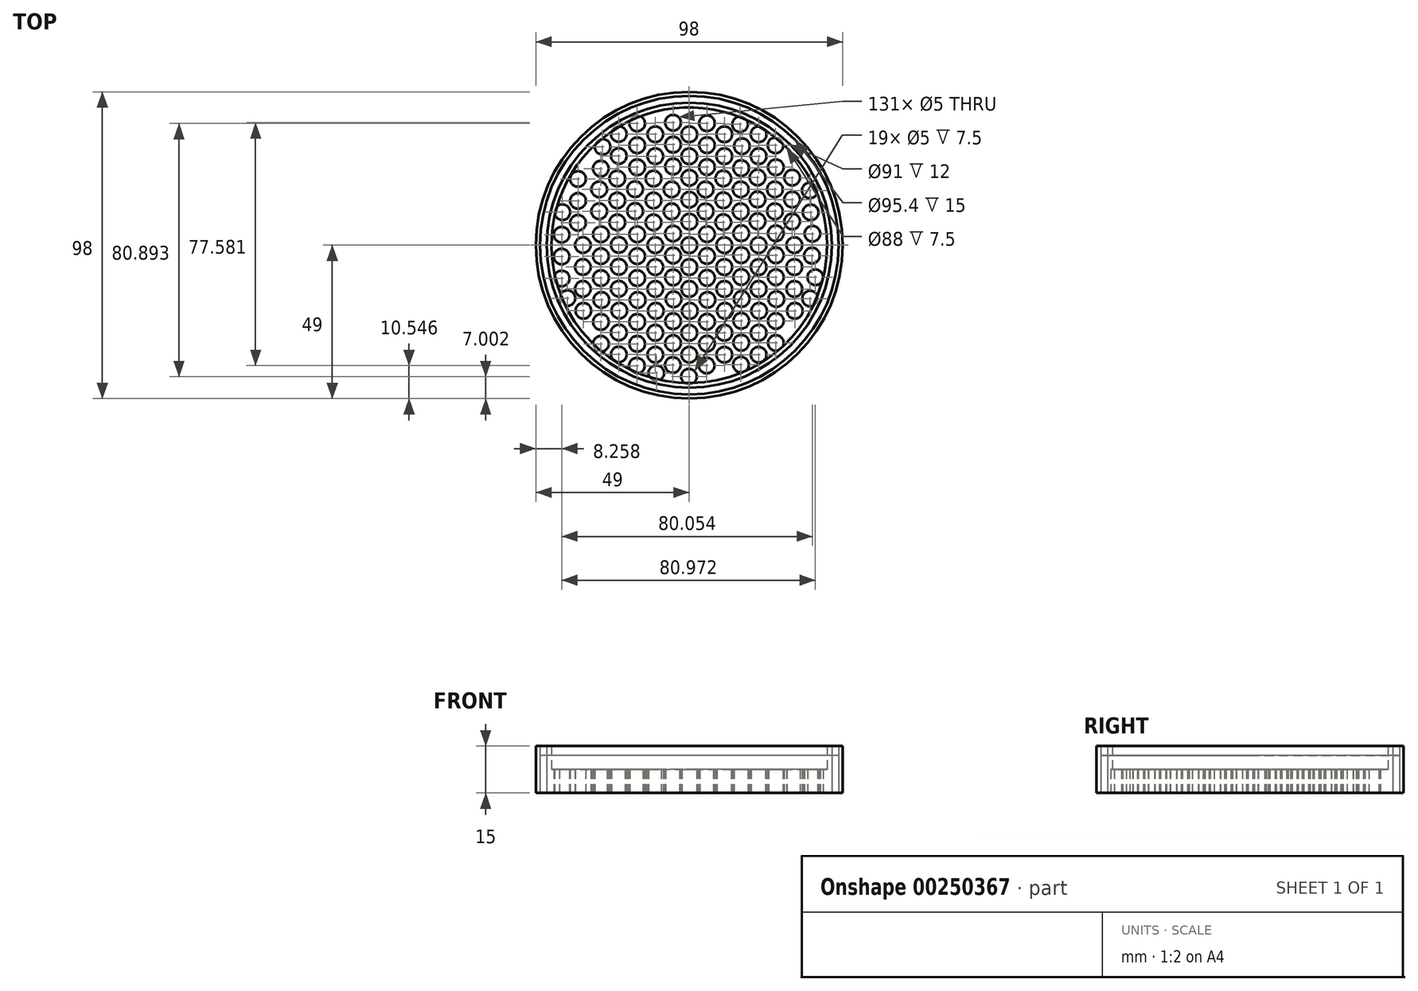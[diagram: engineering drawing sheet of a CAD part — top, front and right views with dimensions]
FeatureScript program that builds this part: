
annotation { "Feature Type Name" : "Feature", "Feature Type Description" : "" }
export const myFeature = defineFeature(function(context is Context, id is Id, definition is map)
    precondition{}
    {
        {
            var Q0;
            Q0=qCreatedBy(makeId("Top.planeOp"),FACE);
            var sketch = newSketch(context, id + "F0", { "sketchPlane" : qUnion([Q0])});
            skCircle(sketch, "E0", {"center": v(0, 0) * mm, "radius": 49 * mm});
            skCircle(sketch, "E1", {"center": v(0, 0) * mm, "radius": 45.5 * mm});
            skCircle(sketch, "E2", {"center": v(0, 0) * mm, "radius": 47.7 * mm});
            skCircle(sketch, "E3", {"center": v(0, 0) * mm, "radius": 44 * mm});
            skSolve(sketch);
        }
        {
            var Q0;
            Q0 = qSketchRegion(id + "F0", true);
            var Q1;
            Q1=makeQuery(id+"F0.imprint","IMPRINT",FACE,{"disambiguationData":[TD([[makeQuery(id+"F0.imprint","IMPRINT",EDGE,{"derivedFrom":sQuery(id+"F0.wireOp",EDGE,"E1")}),1.0]])]});
            extrude(context, id + "F1", {"entities" : qUnion([Q0, Q1]), "depth" : 15 * mm});
        }
        {
            var Q0;
            Q0=makeQuery(id+"F0.imprint","IMPRINT",FACE,{"disambiguationData":[TD([[makeQuery(id+"F0.imprint","IMPRINT",EDGE,{"derivedFrom":sQuery(id+"F0.wireOp",EDGE,"E1")}),-1.0]])]});
            extrude(context, id + "F2", {"entities" : qUnion([Q0]), "depth" : 12 * mm});
        }
        {
            var Q0;
            Q0=makeQuery(id+"F0.imprint","IMPRINT",FACE,{"disambiguationData":[TD([[makeQuery(id+"F0.imprint","IMPRINT",EDGE,{"derivedFrom":sQuery(id+"F0.wireOp",EDGE,"E3")}),1.0]])]});
            extrude(context, id + "F3", {"entities" : qUnion([Q0]), "operationType" : NewBodyOperationType.ADD, "depth" : 7.5 * mm});
        }
        {
            var Q0;
            Q0=qCreatedBy(makeId("Top.planeOp"),FACE);
            var sketch = newSketch(context, id + "F4", { "sketchPlane" : qUnion([Q0])});
            skCircle(sketch, "E4", {"center": v(0, 0) * mm, "radius": 2.5 * mm});
            skCircle(sketch, "E5", {"center": v(0, -7) * mm, "radius": 2.5 * mm});
            skCircle(sketch, "E6", {"center": v(0, -14) * mm, "radius": 2.5 * mm});
            skCircle(sketch, "E7", {"center": v(0.16, -21) * mm, "radius": 2.5 * mm});
            skCircle(sketch, "E8", {"center": v(0, -28) * mm, "radius": 2.5 * mm});
            skCircle(sketch, "E9", {"center": v(0, -35) * mm, "radius": 2.5 * mm});
            skCircle(sketch, "E10", {"center": v(-0.1, -42) * mm, "radius": 2.5 * mm});
            skCircle(sketch, "E11", {"center": v(5.64, 3.54) * mm, "radius": 2.5 * mm});
            skCircle(sketch, "E12", {"center": v(5.64, -3.46) * mm, "radius": 2.5 * mm});
            skCircle(sketch, "E13", {"center": v(5.64, -10.46) * mm, "radius": 2.5 * mm});
            skCircle(sketch, "E14", {"center": v(5.8, -17.45) * mm, "radius": 2.5 * mm});
            skCircle(sketch, "E15", {"center": v(5.64, -24.45) * mm, "radius": 2.5 * mm});
            skCircle(sketch, "E16", {"center": v(5.64, -31.45) * mm, "radius": 2.5 * mm});
            skCircle(sketch, "E17", {"center": v(5.55, -38.45) * mm, "radius": 2.5 * mm});
            skCircle(sketch, "E18", {"center": v(-5.18, 3.72) * mm, "radius": 2.5 * mm});
            skCircle(sketch, "E19", {"center": v(-5.18, -3.28) * mm, "radius": 2.5 * mm});
            skCircle(sketch, "E20", {"center": v(-5.18, -10.28) * mm, "radius": 2.5 * mm});
            skCircle(sketch, "E21", {"center": v(-5.02, -17.28) * mm, "radius": 2.5 * mm});
            skCircle(sketch, "E22", {"center": v(-5.18, -24.28) * mm, "radius": 2.5 * mm});
            skCircle(sketch, "E23", {"center": v(-5.18, -31.28) * mm, "radius": 2.5 * mm});
            skCircle(sketch, "E24", {"center": v(-5.28, -38.28) * mm, "radius": 2.5 * mm});
            skCircle(sketch, "E25", {"center": v(11.2, 0.01) * mm, "radius": 2.5 * mm});
            skCircle(sketch, "E26", {"center": v(11.2, -6.99) * mm, "radius": 2.5 * mm});
            skCircle(sketch, "E27", {"center": v(11.2, -13.99) * mm, "radius": 2.5 * mm});
            skCircle(sketch, "E28", {"center": v(11.36, -20.98) * mm, "radius": 2.5 * mm});
            skCircle(sketch, "E29", {"center": v(11.2, -27.98) * mm, "radius": 2.5 * mm});
            skCircle(sketch, "E30", {"center": v(11.2, -34.98) * mm, "radius": 2.5 * mm});
            skCircle(sketch, "E31", {"center": v(16.58, 3.83) * mm, "radius": 2.5 * mm});
            skCircle(sketch, "E32", {"center": v(16.58, -3.17) * mm, "radius": 2.5 * mm});
            skCircle(sketch, "E33", {"center": v(16.58, -10.17) * mm, "radius": 2.5 * mm});
            skCircle(sketch, "E34", {"center": v(16.74, -17.17) * mm, "radius": 2.5 * mm});
            skCircle(sketch, "E35", {"center": v(16.58, -24.17) * mm, "radius": 2.5 * mm});
            skCircle(sketch, "E36", {"center": v(16.58, -31.17) * mm, "radius": 2.5 * mm});
            skCircle(sketch, "E37", {"center": v(16.48, -38.16) * mm, "radius": 2.5 * mm});
            skCircle(sketch, "E38", {"center": v(22.14, 0.01) * mm, "radius": 2.5 * mm});
            skCircle(sketch, "E39", {"center": v(22.14, -6.99) * mm, "radius": 2.5 * mm});
            skCircle(sketch, "E40", {"center": v(22.14, -13.99) * mm, "radius": 2.5 * mm});
            skCircle(sketch, "E41", {"center": v(22.3, -20.98) * mm, "radius": 2.5 * mm});
            skCircle(sketch, "E42", {"center": v(22.14, -27.98) * mm, "radius": 2.5 * mm});
            skCircle(sketch, "E43", {"center": v(22.14, -34.98) * mm, "radius": 2.5 * mm});
            skCircle(sketch, "E44", {"center": v(27.64, 3.78) * mm, "radius": 2.5 * mm});
            skCircle(sketch, "E45", {"center": v(27.64, -3.22) * mm, "radius": 2.5 * mm});
            skCircle(sketch, "E46", {"center": v(27.64, -10.22) * mm, "radius": 2.5 * mm});
            skCircle(sketch, "E47", {"center": v(27.8, -17.22) * mm, "radius": 2.5 * mm});
            skCircle(sketch, "E48", {"center": v(27.64, -24.22) * mm, "radius": 2.5 * mm});
            skCircle(sketch, "E49", {"center": v(27.64, -31.22) * mm, "radius": 2.5 * mm});
            skCircle(sketch, "E50", {"center": v(33.54, 0.01) * mm, "radius": 2.5 * mm});
            skCircle(sketch, "E51", {"center": v(33.54, -6.99) * mm, "radius": 2.5 * mm});
            skCircle(sketch, "E52", {"center": v(33.54, -13.99) * mm, "radius": 2.5 * mm});
            skCircle(sketch, "E53", {"center": v(33.7, -20.98) * mm, "radius": 2.5 * mm});
            skCircle(sketch, "E54", {"center": v(39.31, 3.67) * mm, "radius": 2.5 * mm});
            skCircle(sketch, "E55", {"center": v(39.15, -3.33) * mm, "radius": 2.5 * mm});
            skCircle(sketch, "E56", {"center": v(40.23, -10.25) * mm, "radius": 2.5 * mm});
            skCircle(sketch, "E57", {"center": v(38.57, -17.05) * mm, "radius": 2.5 * mm});
            skCircle(sketch, "E58", {"center": v(-10.85, 0.01) * mm, "radius": 2.5 * mm});
            skCircle(sketch, "E59", {"center": v(-10.85, -6.99) * mm, "radius": 2.5 * mm});
            skCircle(sketch, "E60", {"center": v(-10.85, -13.99) * mm, "radius": 2.5 * mm});
            skCircle(sketch, "E61", {"center": v(-10.69, -20.98) * mm, "radius": 2.5 * mm});
            skCircle(sketch, "E62", {"center": v(-10.85, -27.98) * mm, "radius": 2.5 * mm});
            skCircle(sketch, "E63", {"center": v(-10.85, -34.98) * mm, "radius": 2.5 * mm});
            skCircle(sketch, "E64", {"center": v(-16.63, 3.49) * mm, "radius": 2.5 * mm});
            skCircle(sketch, "E65", {"center": v(-16.63, -3.51) * mm, "radius": 2.5 * mm});
            skCircle(sketch, "E66", {"center": v(-16.63, -10.51) * mm, "radius": 2.5 * mm});
            skCircle(sketch, "E67", {"center": v(-16.47, -17.51) * mm, "radius": 2.5 * mm});
            skCircle(sketch, "E68", {"center": v(-16.63, -24.51) * mm, "radius": 2.5 * mm});
            skCircle(sketch, "E69", {"center": v(-16.63, -31.51) * mm, "radius": 2.5 * mm});
            skCircle(sketch, "E70", {"center": v(-16.73, -38.51) * mm, "radius": 2.5 * mm});
            skCircle(sketch, "E71", {"center": v(-22.5, 0.1) * mm, "radius": 2.5 * mm});
            skCircle(sketch, "E72", {"center": v(-22.5, -6.9) * mm, "radius": 2.5 * mm});
            skCircle(sketch, "E73", {"center": v(-22.5, -13.9) * mm, "radius": 2.5 * mm});
            skCircle(sketch, "E74", {"center": v(-22.34, -20.9) * mm, "radius": 2.5 * mm});
            skCircle(sketch, "E75", {"center": v(-22.5, -27.9) * mm, "radius": 2.5 * mm});
            skCircle(sketch, "E76", {"center": v(-22.5, -34.9) * mm, "radius": 2.5 * mm});
            skCircle(sketch, "E77", {"center": v(-28.21, 3.49) * mm, "radius": 2.5 * mm});
            skCircle(sketch, "E78", {"center": v(-28.21, -3.51) * mm, "radius": 2.5 * mm});
            skCircle(sketch, "E79", {"center": v(-28.21, -10.51) * mm, "radius": 2.5 * mm});
            skCircle(sketch, "E80", {"center": v(-28.05, -17.51) * mm, "radius": 2.5 * mm});
            skCircle(sketch, "E81", {"center": v(-28.21, -24.51) * mm, "radius": 2.5 * mm});
            skCircle(sketch, "E82", {"center": v(-28.21, -31.51) * mm, "radius": 2.5 * mm});
            skCircle(sketch, "E83", {"center": v(-33.98, 0.04) * mm, "radius": 2.5 * mm});
            skCircle(sketch, "E84", {"center": v(-33.98, -6.96) * mm, "radius": 2.5 * mm});
            skCircle(sketch, "E85", {"center": v(-33.98, -13.96) * mm, "radius": 2.5 * mm});
            skCircle(sketch, "E86", {"center": v(-33.82, -20.96) * mm, "radius": 2.5 * mm});
            skCircle(sketch, "E87", {"center": v(-40.74, 3.36) * mm, "radius": 2.5 * mm});
            skCircle(sketch, "E88", {"center": v(-40.74, -3.64) * mm, "radius": 2.5 * mm});
            skCircle(sketch, "E89", {"center": v(-40.74, -10.64) * mm, "radius": 2.5 * mm});
            skCircle(sketch, "E90", {"center": v(-10.53, -40.88) * mm, "radius": 2.5 * mm});
            skCircle(sketch, "E91", {"center": v(5.21, 17.8) * mm, "radius": 2.5 * mm});
            skCircle(sketch, "E92", {"center": v(5.21, 10.8) * mm, "radius": 2.5 * mm});
            skCircle(sketch, "E93", {"center": v(10.86, 21.34) * mm, "radius": 2.5 * mm});
            skCircle(sketch, "E94", {"center": v(10.86, 14.34) * mm, "radius": 2.5 * mm});
            skCircle(sketch, "E95", {"center": v(10.86, 7.34) * mm, "radius": 2.5 * mm});
            skCircle(sketch, "E96", {"center": v(0.03, 21.51) * mm, "radius": 2.5 * mm});
            skCircle(sketch, "E97", {"center": v(0.03, 14.51) * mm, "radius": 2.5 * mm});
            skCircle(sketch, "E98", {"center": v(0.03, 7.51) * mm, "radius": 2.5 * mm});
            skCircle(sketch, "E99", {"center": v(16.41, 17.8) * mm, "radius": 2.5 * mm});
            skCircle(sketch, "E100", {"center": v(16.41, 10.8) * mm, "radius": 2.5 * mm});
            skCircle(sketch, "E101", {"center": v(21.8, 21.63) * mm, "radius": 2.5 * mm});
            skCircle(sketch, "E102", {"center": v(21.8, 14.63) * mm, "radius": 2.5 * mm});
            skCircle(sketch, "E103", {"center": v(21.8, 7.63) * mm, "radius": 2.5 * mm});
            skCircle(sketch, "E104", {"center": v(27.35, 17.8) * mm, "radius": 2.5 * mm});
            skCircle(sketch, "E105", {"center": v(27.35, 10.8) * mm, "radius": 2.5 * mm});
            skCircle(sketch, "E106", {"center": v(32.85, 21.57) * mm, "radius": 2.5 * mm});
            skCircle(sketch, "E107", {"center": v(32.85, 14.57) * mm, "radius": 2.5 * mm});
            skCircle(sketch, "E108", {"center": v(32.85, 7.57) * mm, "radius": 2.5 * mm});
            skCircle(sketch, "E109", {"center": v(38.49, 17.5) * mm, "radius": 2.5 * mm});
            skCircle(sketch, "E110", {"center": v(38.75, 10.5) * mm, "radius": 2.5 * mm});
            skCircle(sketch, "E111", {"center": v(-5.64, 17.8) * mm, "radius": 2.5 * mm});
            skCircle(sketch, "E112", {"center": v(-5.64, 10.8) * mm, "radius": 2.5 * mm});
            skCircle(sketch, "E113", {"center": v(-11.42, 21.28) * mm, "radius": 2.5 * mm});
            skCircle(sketch, "E114", {"center": v(-11.42, 14.28) * mm, "radius": 2.5 * mm});
            skCircle(sketch, "E115", {"center": v(-11.42, 7.28) * mm, "radius": 2.5 * mm});
            skCircle(sketch, "E116", {"center": v(-17.3, 17.89) * mm, "radius": 2.5 * mm});
            skCircle(sketch, "E117", {"center": v(-17.3, 10.89) * mm, "radius": 2.5 * mm});
            skCircle(sketch, "E118", {"center": v(-23, 21.28) * mm, "radius": 2.5 * mm});
            skCircle(sketch, "E119", {"center": v(-23, 14.28) * mm, "radius": 2.5 * mm});
            skCircle(sketch, "E120", {"center": v(-23, 7.28) * mm, "radius": 2.5 * mm});
            skCircle(sketch, "E121", {"center": v(-28.77, 17.84) * mm, "radius": 2.5 * mm});
            skCircle(sketch, "E122", {"center": v(-28.77, 10.84) * mm, "radius": 2.5 * mm});
            skCircle(sketch, "E123", {"center": v(-35.53, 21.16) * mm, "radius": 2.5 * mm});
            skCircle(sketch, "E124", {"center": v(-35.53, 14.16) * mm, "radius": 2.5 * mm});
            skCircle(sketch, "E125", {"center": v(-35.53, 7.16) * mm, "radius": 2.5 * mm});
            skCircle(sketch, "E126", {"center": v(0, 35.4) * mm, "radius": 2.5 * mm});
            skCircle(sketch, "E127", {"center": v(0, 28.4) * mm, "radius": 2.5 * mm});
            skCircle(sketch, "E128", {"center": v(5.64, 38.95) * mm, "radius": 2.5 * mm});
            skCircle(sketch, "E129", {"center": v(5.64, 31.95) * mm, "radius": 2.5 * mm});
            skCircle(sketch, "E130", {"center": v(5.64, 24.95) * mm, "radius": 2.5 * mm});
            skCircle(sketch, "E131", {"center": v(-5.18, 39.13) * mm, "radius": 2.5 * mm});
            skCircle(sketch, "E132", {"center": v(-5.18, 32.13) * mm, "radius": 2.5 * mm});
            skCircle(sketch, "E133", {"center": v(-5.18, 25.13) * mm, "radius": 2.5 * mm});
            skCircle(sketch, "E134", {"center": v(11.2, 35.42) * mm, "radius": 2.5 * mm});
            skCircle(sketch, "E135", {"center": v(11.2, 28.42) * mm, "radius": 2.5 * mm});
            skCircle(sketch, "E136", {"center": v(16.2, 38.63) * mm, "radius": 2.5 * mm});
            skCircle(sketch, "E137", {"center": v(16.8, 31.63) * mm, "radius": 2.5 * mm});
            skCircle(sketch, "E138", {"center": v(16.56, 24.64) * mm, "radius": 2.5 * mm});
            skCircle(sketch, "E139", {"center": v(22.13, 35.42) * mm, "radius": 2.5 * mm});
            skCircle(sketch, "E140", {"center": v(22.13, 28.42) * mm, "radius": 2.5 * mm});
            skCircle(sketch, "E141", {"center": v(27.52, 31.9) * mm, "radius": 2.5 * mm});
            skCircle(sketch, "E142", {"center": v(27.64, 24.9) * mm, "radius": 2.5 * mm});
            skCircle(sketch, "E143", {"center": v(-10.85, 35.42) * mm, "radius": 2.5 * mm});
            skCircle(sketch, "E144", {"center": v(-10.85, 28.42) * mm, "radius": 2.5 * mm});
            skCircle(sketch, "E145", {"center": v(-16.64, 38.9) * mm, "radius": 2.5 * mm});
            skCircle(sketch, "E146", {"center": v(-16.64, 31.9) * mm, "radius": 2.5 * mm});
            skCircle(sketch, "E147", {"center": v(-16.64, 24.9) * mm, "radius": 2.5 * mm});
            skCircle(sketch, "E148", {"center": v(-22.5, 35.5) * mm, "radius": 2.5 * mm});
            skCircle(sketch, "E149", {"center": v(-22.5, 28.5) * mm, "radius": 2.5 * mm});
            skCircle(sketch, "E150", {"center": v(-27.7, 31.44) * mm, "radius": 2.5 * mm});
            skCircle(sketch, "E151", {"center": v(-28.25, 24.46) * mm, "radius": 2.5 * mm});
            skCircle(sketch, "E152", {"center": v(-38.9, -16.92) * mm, "radius": 2.5 * mm});
            skCircle(sketch, "E153", {"center": v(-40.55, 10.56) * mm, "radius": 2.5 * mm});
            skSolve(sketch);
        }
        {
            var Q0;
            Q0=makeQuery(id+"F4.imprint","IMPRINT",FACE,{"disambiguationData":[TD([[makeQuery(id+"F4.imprint","IMPRINT",EDGE,{"derivedFrom":sQuery(id+"F4.wireOp",EDGE,"E39")}),1.0]])]});
            var Q1;
            Q1=makeQuery(id+"F4.imprint","IMPRINT",FACE,{"disambiguationData":[TD([[makeQuery(id+"F4.imprint","IMPRINT",EDGE,{"derivedFrom":sQuery(id+"F4.wireOp",EDGE,"E145")}),1.0]])]});
            var Q2;
            Q2=makeQuery(id+"F4.imprint","IMPRINT",FACE,{"disambiguationData":[TD([[makeQuery(id+"F4.imprint","IMPRINT",EDGE,{"derivedFrom":sQuery(id+"F4.wireOp",EDGE,"E23")}),1.0]])]});
            var Q3;
            Q3=makeQuery(id+"F4.imprint","IMPRINT",FACE,{"disambiguationData":[TD([[makeQuery(id+"F4.imprint","IMPRINT",EDGE,{"derivedFrom":sQuery(id+"F4.wireOp",EDGE,"E41")}),1.0]])]});
            var Q4;
            Q4=makeQuery(id+"F4.imprint","IMPRINT",FACE,{"disambiguationData":[TD([[makeQuery(id+"F4.imprint","IMPRINT",EDGE,{"derivedFrom":sQuery(id+"F4.wireOp",EDGE,"E119")}),1.0]])]});
            var Q5;
            Q5=makeQuery(id+"F4.imprint","IMPRINT",FACE,{"disambiguationData":[TD([[makeQuery(id+"F4.imprint","IMPRINT",EDGE,{"derivedFrom":sQuery(id+"F4.wireOp",EDGE,"E87")}),1.0]])]});
            var Q6;
            Q6=makeQuery(id+"F4.imprint","IMPRINT",FACE,{"disambiguationData":[TD([[makeQuery(id+"F4.imprint","IMPRINT",EDGE,{"derivedFrom":sQuery(id+"F4.wireOp",EDGE,"E71")}),1.0]])]});
            var Q7;
            Q7=makeQuery(id+"F4.imprint","IMPRINT",FACE,{"disambiguationData":[TD([[makeQuery(id+"F4.imprint","IMPRINT",EDGE,{"derivedFrom":sQuery(id+"F4.wireOp",EDGE,"E21")}),1.0]])]});
            var Q8;
            Q8=makeQuery(id+"F4.imprint","IMPRINT",FACE,{"disambiguationData":[TD([[makeQuery(id+"F4.imprint","IMPRINT",EDGE,{"derivedFrom":sQuery(id+"F4.wireOp",EDGE,"E135")}),1.0]])]});
            var Q9;
            Q9=makeQuery(id+"F4.imprint","IMPRINT",FACE,{"disambiguationData":[TD([[makeQuery(id+"F4.imprint","IMPRINT",EDGE,{"derivedFrom":sQuery(id+"F4.wireOp",EDGE,"E151")}),1.0]])]});
            var Q10;
            Q10=makeQuery(id+"F4.imprint","IMPRINT",FACE,{"disambiguationData":[TD([[makeQuery(id+"F4.imprint","IMPRINT",EDGE,{"derivedFrom":sQuery(id+"F4.wireOp",EDGE,"E36")}),1.0]])]});
            var Q11;
            Q11=makeQuery(id+"F4.imprint","IMPRINT",FACE,{"disambiguationData":[TD([[makeQuery(id+"F4.imprint","IMPRINT",EDGE,{"derivedFrom":sQuery(id+"F4.wireOp",EDGE,"E132")}),1.0]])]});
            var Q12;
            Q12=makeQuery(id+"F4.imprint","IMPRINT",FACE,{"disambiguationData":[TD([[makeQuery(id+"F4.imprint","IMPRINT",EDGE,{"derivedFrom":sQuery(id+"F4.wireOp",EDGE,"E37")}),1.0]])]});
            var Q13;
            Q13=makeQuery(id+"F4.imprint","IMPRINT",FACE,{"disambiguationData":[TD([[makeQuery(id+"F4.imprint","IMPRINT",EDGE,{"derivedFrom":sQuery(id+"F4.wireOp",EDGE,"E148")}),1.0]])]});
            var Q14;
            Q14=makeQuery(id+"F4.imprint","IMPRINT",FACE,{"disambiguationData":[TD([[makeQuery(id+"F4.imprint","IMPRINT",EDGE,{"derivedFrom":sQuery(id+"F4.wireOp",EDGE,"E53")}),1.0]])]});
            var Q15;
            Q15=makeQuery(id+"F4.imprint","IMPRINT",FACE,{"disambiguationData":[TD([[makeQuery(id+"F4.imprint","IMPRINT",EDGE,{"derivedFrom":sQuery(id+"F4.wireOp",EDGE,"E73")}),1.0]])]});
            var Q16;
            Q16=makeQuery(id+"F4.imprint","IMPRINT",FACE,{"disambiguationData":[TD([[makeQuery(id+"F4.imprint","IMPRINT",EDGE,{"derivedFrom":sQuery(id+"F4.wireOp",EDGE,"E105")}),1.0]])]});
            var Q17;
            Q17=makeQuery(id+"F4.imprint","IMPRINT",FACE,{"disambiguationData":[TD([[makeQuery(id+"F4.imprint","IMPRINT",EDGE,{"derivedFrom":sQuery(id+"F4.wireOp",EDGE,"E68")}),1.0]])]});
            var Q18;
            Q18=makeQuery(id+"F4.imprint","IMPRINT",FACE,{"disambiguationData":[TD([[makeQuery(id+"F4.imprint","IMPRINT",EDGE,{"derivedFrom":sQuery(id+"F4.wireOp",EDGE,"E84")}),1.0]])]});
            var Q19;
            Q19=makeQuery(id+"F4.imprint","IMPRINT",FACE,{"disambiguationData":[TD([[makeQuery(id+"F4.imprint","IMPRINT",EDGE,{"derivedFrom":sQuery(id+"F4.wireOp",EDGE,"E103")}),1.0]])]});
            var Q20;
            Q20=makeQuery(id+"F4.imprint","IMPRINT",FACE,{"disambiguationData":[TD([[makeQuery(id+"F4.imprint","IMPRINT",EDGE,{"derivedFrom":sQuery(id+"F4.wireOp",EDGE,"E20")}),1.0]])]});
            var Q21;
            Q21=makeQuery(id+"F4.imprint","IMPRINT",FACE,{"disambiguationData":[TD([[makeQuery(id+"F4.imprint","IMPRINT",EDGE,{"derivedFrom":sQuery(id+"F4.wireOp",EDGE,"E116")}),1.0]])]});
            var Q22;
            Q22=makeQuery(id+"F4.imprint","IMPRINT",FACE,{"disambiguationData":[TD([[makeQuery(id+"F4.imprint","IMPRINT",EDGE,{"derivedFrom":sQuery(id+"F4.wireOp",EDGE,"E100")}),1.0]])]});
            var Q23;
            Q23=makeQuery(id+"F4.imprint","IMPRINT",FACE,{"disambiguationData":[TD([[makeQuery(id+"F4.imprint","IMPRINT",EDGE,{"derivedFrom":sQuery(id+"F4.wireOp",EDGE,"E101")}),1.0]])]});
            var Q24;
            Q24=makeQuery(id+"F4.imprint","IMPRINT",FACE,{"disambiguationData":[TD([[makeQuery(id+"F4.imprint","IMPRINT",EDGE,{"derivedFrom":sQuery(id+"F4.wireOp",EDGE,"E89")}),1.0]])]});
            var Q25;
            Q25=makeQuery(id+"F4.imprint","IMPRINT",FACE,{"disambiguationData":[TD([[makeQuery(id+"F4.imprint","IMPRINT",EDGE,{"derivedFrom":sQuery(id+"F4.wireOp",EDGE,"E81")}),1.0]])]});
            var Q26;
            Q26=makeQuery(id+"F4.imprint","IMPRINT",FACE,{"disambiguationData":[TD([[makeQuery(id+"F4.imprint","IMPRINT",EDGE,{"derivedFrom":sQuery(id+"F4.wireOp",EDGE,"E85")}),1.0]])]});
            var Q27;
            Q27=makeQuery(id+"F4.imprint","IMPRINT",FACE,{"disambiguationData":[TD([[makeQuery(id+"F4.imprint","IMPRINT",EDGE,{"derivedFrom":sQuery(id+"F4.wireOp",EDGE,"E153")}),1.0]])]});
            var Q28;
            Q28=makeQuery(id+"F4.imprint","IMPRINT",FACE,{"disambiguationData":[TD([[makeQuery(id+"F4.imprint","IMPRINT",EDGE,{"derivedFrom":sQuery(id+"F4.wireOp",EDGE,"E117")}),1.0]])]});
            var Q29;
            Q29=makeQuery(id+"F4.imprint","IMPRINT",FACE,{"disambiguationData":[TD([[makeQuery(id+"F4.imprint","IMPRINT",EDGE,{"derivedFrom":sQuery(id+"F4.wireOp",EDGE,"E69")}),1.0]])]});
            var Q30;
            Q30=makeQuery(id+"F4.imprint","IMPRINT",FACE,{"disambiguationData":[TD([[makeQuery(id+"F4.imprint","IMPRINT",EDGE,{"derivedFrom":sQuery(id+"F4.wireOp",EDGE,"E149")}),1.0]])]});
            var Q31;
            Q31=makeQuery(id+"F4.imprint","IMPRINT",FACE,{"disambiguationData":[TD([[makeQuery(id+"F4.imprint","IMPRINT",EDGE,{"derivedFrom":sQuery(id+"F4.wireOp",EDGE,"E133")}),1.0]])]});
            var Q32;
            Q32=makeQuery(id+"F4.imprint","IMPRINT",FACE,{"disambiguationData":[TD([[makeQuery(id+"F4.imprint","IMPRINT",EDGE,{"derivedFrom":sQuery(id+"F4.wireOp",EDGE,"E54")}),1.0]])]});
            var Q33;
            Q33=makeQuery(id+"F4.imprint","IMPRINT",FACE,{"disambiguationData":[TD([[makeQuery(id+"F4.imprint","IMPRINT",EDGE,{"derivedFrom":sQuery(id+"F4.wireOp",EDGE,"E38")}),1.0]])]});
            var Q34;
            Q34=makeQuery(id+"F4.imprint","IMPRINT",FACE,{"disambiguationData":[TD([[makeQuery(id+"F4.imprint","IMPRINT",EDGE,{"derivedFrom":sQuery(id+"F4.wireOp",EDGE,"E22")}),1.0]])]});
            var Q35;
            Q35=makeQuery(id+"F4.imprint","IMPRINT",FACE,{"disambiguationData":[TD([[makeQuery(id+"F4.imprint","IMPRINT",EDGE,{"derivedFrom":sQuery(id+"F4.wireOp",EDGE,"E118")}),1.0]])]});
            var Q36;
            Q36=makeQuery(id+"F4.imprint","IMPRINT",FACE,{"disambiguationData":[TD([[makeQuery(id+"F4.imprint","IMPRINT",EDGE,{"derivedFrom":sQuery(id+"F4.wireOp",EDGE,"E86")}),1.0]])]});
            var Q37;
            Q37=makeQuery(id+"F4.imprint","IMPRINT",FACE,{"disambiguationData":[TD([[makeQuery(id+"F4.imprint","IMPRINT",EDGE,{"derivedFrom":sQuery(id+"F4.wireOp",EDGE,"E102")}),1.0]])]});
            var Q38;
            Q38=makeQuery(id+"F4.imprint","IMPRINT",FACE,{"disambiguationData":[TD([[makeQuery(id+"F4.imprint","IMPRINT",EDGE,{"derivedFrom":sQuery(id+"F4.wireOp",EDGE,"E137")}),1.0]])]});
            var Q39;
            Q39=makeQuery(id+"F4.imprint","IMPRINT",FACE,{"disambiguationData":[TD([[makeQuery(id+"F4.imprint","IMPRINT",EDGE,{"derivedFrom":sQuery(id+"F4.wireOp",EDGE,"E65")}),1.0]])]});
            var Q40;
            Q40=makeQuery(id+"F4.imprint","IMPRINT",FACE,{"disambiguationData":[TD([[makeQuery(id+"F4.imprint","IMPRINT",EDGE,{"derivedFrom":sQuery(id+"F4.wireOp",EDGE,"E70")}),1.0]])]});
            var Q41;
            Q41=makeQuery(id+"F4.imprint","IMPRINT",FACE,{"disambiguationData":[TD([[makeQuery(id+"F4.imprint","IMPRINT",EDGE,{"derivedFrom":sQuery(id+"F4.wireOp",EDGE,"E134")}),1.0]])]});
            var Q42;
            Q42=makeQuery(id+"F4.imprint","IMPRINT",FACE,{"disambiguationData":[TD([[makeQuery(id+"F4.imprint","IMPRINT",EDGE,{"derivedFrom":sQuery(id+"F4.wireOp",EDGE,"E52")}),1.0]])]});
            var Q43;
            Q43=makeQuery(id+"F4.imprint","IMPRINT",FACE,{"disambiguationData":[TD([[makeQuery(id+"F4.imprint","IMPRINT",EDGE,{"derivedFrom":sQuery(id+"F4.wireOp",EDGE,"E121")}),1.0]])]});
            var Q44;
            Q44=makeQuery(id+"F4.imprint","IMPRINT",FACE,{"disambiguationData":[TD([[makeQuery(id+"F4.imprint","IMPRINT",EDGE,{"derivedFrom":sQuery(id+"F4.wireOp",EDGE,"E25")}),1.0]])]});
            var Q45;
            Q45=makeQuery(id+"F4.imprint","IMPRINT",FACE,{"disambiguationData":[TD([[makeQuery(id+"F4.imprint","IMPRINT",EDGE,{"derivedFrom":sQuery(id+"F4.wireOp",EDGE,"E55")}),1.0]])]});
            var Q46;
            Q46=makeQuery(id+"F4.imprint","IMPRINT",FACE,{"disambiguationData":[TD([[makeQuery(id+"F4.imprint","IMPRINT",EDGE,{"derivedFrom":sQuery(id+"F4.wireOp",EDGE,"E150")}),1.0]])]});
            var Q47;
            Q47=makeQuery(id+"F4.imprint","IMPRINT",FACE,{"disambiguationData":[TD([[makeQuery(id+"F4.imprint","IMPRINT",EDGE,{"derivedFrom":sQuery(id+"F4.wireOp",EDGE,"E57")}),1.0]])]});
            var Q48;
            Q48=makeQuery(id+"F4.imprint","IMPRINT",FACE,{"disambiguationData":[TD([[makeQuery(id+"F4.imprint","IMPRINT",EDGE,{"derivedFrom":sQuery(id+"F4.wireOp",EDGE,"E26")}),1.0]])]});
            var Q49;
            Q49=makeQuery(id+"F4.imprint","IMPRINT",FACE,{"disambiguationData":[TD([[makeQuery(id+"F4.imprint","IMPRINT",EDGE,{"derivedFrom":sQuery(id+"F4.wireOp",EDGE,"E56")}),1.0]])]});
            var Q50;
            Q50=makeQuery(id+"F4.imprint","IMPRINT",FACE,{"disambiguationData":[TD([[makeQuery(id+"F4.imprint","IMPRINT",EDGE,{"derivedFrom":sQuery(id+"F4.wireOp",EDGE,"E90")}),1.0]])]});
            var Q51;
            Q51=makeQuery(id+"F4.imprint","IMPRINT",FACE,{"disambiguationData":[TD([[makeQuery(id+"F4.imprint","IMPRINT",EDGE,{"derivedFrom":sQuery(id+"F4.wireOp",EDGE,"E74")}),1.0]])]});
            var Q52;
            Q52=makeQuery(id+"F4.imprint","IMPRINT",FACE,{"disambiguationData":[TD([[makeQuery(id+"F4.imprint","IMPRINT",EDGE,{"derivedFrom":sQuery(id+"F4.wireOp",EDGE,"E42")}),1.0]])]});
            var Q53;
            Q53=makeQuery(id+"F4.imprint","IMPRINT",FACE,{"disambiguationData":[TD([[makeQuery(id+"F4.imprint","IMPRINT",EDGE,{"derivedFrom":sQuery(id+"F4.wireOp",EDGE,"E58")}),1.0]])]});
            var Q54;
            Q54=makeQuery(id+"F4.imprint","IMPRINT",FACE,{"disambiguationData":[TD([[makeQuery(id+"F4.imprint","IMPRINT",EDGE,{"derivedFrom":sQuery(id+"F4.wireOp",EDGE,"E40")}),1.0]])]});
            var Q55;
            Q55=makeQuery(id+"F4.imprint","IMPRINT",FACE,{"disambiguationData":[TD([[makeQuery(id+"F4.imprint","IMPRINT",EDGE,{"derivedFrom":sQuery(id+"F4.wireOp",EDGE,"E122")}),1.0]])]});
            var Q56;
            Q56=makeQuery(id+"F4.imprint","IMPRINT",FACE,{"disambiguationData":[TD([[makeQuery(id+"F4.imprint","IMPRINT",EDGE,{"derivedFrom":sQuery(id+"F4.wireOp",EDGE,"E24")}),1.0]])]});
            var Q57;
            Q57=makeQuery(id+"F4.imprint","IMPRINT",FACE,{"disambiguationData":[TD([[makeQuery(id+"F4.imprint","IMPRINT",EDGE,{"derivedFrom":sQuery(id+"F4.wireOp",EDGE,"E106")}),1.0]])]});
            var Q58;
            Q58=makeQuery(id+"F4.imprint","IMPRINT",FACE,{"disambiguationData":[TD([[makeQuery(id+"F4.imprint","IMPRINT",EDGE,{"derivedFrom":sQuery(id+"F4.wireOp",EDGE,"E138")}),1.0]])]});
            var Q59;
            Q59=makeQuery(id+"F4.imprint","IMPRINT",FACE,{"disambiguationData":[TD([[makeQuery(id+"F4.imprint","IMPRINT",EDGE,{"derivedFrom":sQuery(id+"F4.wireOp",EDGE,"E120")}),1.0]])]});
            var Q60;
            Q60=makeQuery(id+"F4.imprint","IMPRINT",FACE,{"disambiguationData":[TD([[makeQuery(id+"F4.imprint","IMPRINT",EDGE,{"derivedFrom":sQuery(id+"F4.wireOp",EDGE,"E88")}),1.0]])]});
            var Q61;
            Q61=makeQuery(id+"F4.imprint","IMPRINT",FACE,{"disambiguationData":[TD([[makeQuery(id+"F4.imprint","IMPRINT",EDGE,{"derivedFrom":sQuery(id+"F4.wireOp",EDGE,"E104")}),1.0]])]});
            var Q62;
            Q62=makeQuery(id+"F4.imprint","IMPRINT",FACE,{"disambiguationData":[TD([[makeQuery(id+"F4.imprint","IMPRINT",EDGE,{"derivedFrom":sQuery(id+"F4.wireOp",EDGE,"E91")}),1.0]])]});
            var Q63;
            Q63=makeQuery(id+"F4.imprint","IMPRINT",FACE,{"disambiguationData":[TD([[makeQuery(id+"F4.imprint","IMPRINT",EDGE,{"derivedFrom":sQuery(id+"F4.wireOp",EDGE,"E72")}),1.0]])]});
            var Q64;
            Q64=makeQuery(id+"F4.imprint","IMPRINT",FACE,{"disambiguationData":[TD([[makeQuery(id+"F4.imprint","IMPRINT",EDGE,{"derivedFrom":sQuery(id+"F4.wireOp",EDGE,"E152")}),1.0]])]});
            var Q65;
            Q65=makeQuery(id+"F4.imprint","IMPRINT",FACE,{"disambiguationData":[TD([[makeQuery(id+"F4.imprint","IMPRINT",EDGE,{"derivedFrom":sQuery(id+"F4.wireOp",EDGE,"E75")}),1.0]])]});
            var Q66;
            Q66=makeQuery(id+"F4.imprint","IMPRINT",FACE,{"disambiguationData":[TD([[makeQuery(id+"F4.imprint","IMPRINT",EDGE,{"derivedFrom":sQuery(id+"F4.wireOp",EDGE,"E136")}),1.0]])]});
            var Q67;
            Q67=makeQuery(id+"F4.imprint","IMPRINT",FACE,{"disambiguationData":[TD([[makeQuery(id+"F4.imprint","IMPRINT",EDGE,{"derivedFrom":sQuery(id+"F4.wireOp",EDGE,"E59")}),1.0]])]});
            var Q68;
            Q68=makeQuery(id+"F4.imprint","IMPRINT",FACE,{"disambiguationData":[TD([[makeQuery(id+"F4.imprint","IMPRINT",EDGE,{"derivedFrom":sQuery(id+"F4.wireOp",EDGE,"E43")}),1.0]])]});
            var Q69;
            Q69=makeQuery(id+"F4.imprint","IMPRINT",FACE,{"disambiguationData":[TD([[makeQuery(id+"F4.imprint","IMPRINT",EDGE,{"derivedFrom":sQuery(id+"F4.wireOp",EDGE,"E139")}),1.0]])]});
            var Q70;
            Q70=makeQuery(id+"F4.imprint","IMPRINT",FACE,{"disambiguationData":[TD([[makeQuery(id+"F4.imprint","IMPRINT",EDGE,{"derivedFrom":sQuery(id+"F4.wireOp",EDGE,"E123")}),1.0]])]});
            var Q71;
            Q71=makeQuery(id+"F4.imprint","IMPRINT",FACE,{"disambiguationData":[TD([[makeQuery(id+"F4.imprint","IMPRINT",EDGE,{"derivedFrom":sQuery(id+"F4.wireOp",EDGE,"E107")}),1.0]])]});
            var Q72;
            Q72=makeQuery(id+"F4.imprint","IMPRINT",FACE,{"disambiguationData":[TD([[makeQuery(id+"F4.imprint","IMPRINT",EDGE,{"derivedFrom":sQuery(id+"F4.wireOp",EDGE,"E27")}),1.0]])]});
            var Q73;
            Q73=makeQuery(id+"F4.imprint","IMPRINT",FACE,{"disambiguationData":[TD([[makeQuery(id+"F4.imprint","IMPRINT",EDGE,{"derivedFrom":sQuery(id+"F4.wireOp",EDGE,"E140")}),1.0]])]});
            var Q74;
            Q74=makeQuery(id+"F4.imprint","IMPRINT",FACE,{"disambiguationData":[TD([[makeQuery(id+"F4.imprint","IMPRINT",EDGE,{"derivedFrom":sQuery(id+"F4.wireOp",EDGE,"E124")}),1.0]])]});
            var Q75;
            Q75=makeQuery(id+"F4.imprint","IMPRINT",FACE,{"disambiguationData":[TD([[makeQuery(id+"F4.imprint","IMPRINT",EDGE,{"derivedFrom":sQuery(id+"F4.wireOp",EDGE,"E108")}),1.0]])]});
            var Q76;
            Q76=makeQuery(id+"F4.imprint","IMPRINT",FACE,{"disambiguationData":[TD([[makeQuery(id+"F4.imprint","IMPRINT",EDGE,{"derivedFrom":sQuery(id+"F4.wireOp",EDGE,"E28")}),1.0]])]});
            var Q77;
            Q77=makeQuery(id+"F4.imprint","IMPRINT",FACE,{"disambiguationData":[TD([[makeQuery(id+"F4.imprint","IMPRINT",EDGE,{"derivedFrom":sQuery(id+"F4.wireOp",EDGE,"E92")}),1.0]])]});
            var Q78;
            Q78=makeQuery(id+"F4.imprint","IMPRINT",FACE,{"disambiguationData":[TD([[makeQuery(id+"F4.imprint","IMPRINT",EDGE,{"derivedFrom":sQuery(id+"F4.wireOp",EDGE,"E76")}),1.0]])]});
            var Q79;
            Q79=makeQuery(id+"F4.imprint","IMPRINT",FACE,{"disambiguationData":[TD([[makeQuery(id+"F4.imprint","IMPRINT",EDGE,{"derivedFrom":sQuery(id+"F4.wireOp",EDGE,"E60")}),1.0]])]});
            var Q80;
            Q80=makeQuery(id+"F4.imprint","IMPRINT",FACE,{"disambiguationData":[TD([[makeQuery(id+"F4.imprint","IMPRINT",EDGE,{"derivedFrom":sQuery(id+"F4.wireOp",EDGE,"E44")}),1.0]])]});
            var Q81;
            Q81=makeQuery(id+"F4.imprint","IMPRINT",FACE,{"disambiguationData":[TD([[makeQuery(id+"F4.imprint","IMPRINT",EDGE,{"derivedFrom":sQuery(id+"F4.wireOp",EDGE,"E147")}),1.0]])]});
            var Q82;
            Q82=makeQuery(id+"F4.imprint","IMPRINT",FACE,{"disambiguationData":[TD([[makeQuery(id+"F4.imprint","IMPRINT",EDGE,{"derivedFrom":sQuery(id+"F4.wireOp",EDGE,"E29")}),1.0]])]});
            var Q83;
            Q83=makeQuery(id+"F4.imprint","IMPRINT",FACE,{"disambiguationData":[TD([[makeQuery(id+"F4.imprint","IMPRINT",EDGE,{"derivedFrom":sQuery(id+"F4.wireOp",EDGE,"E67")}),1.0]])]});
            var Q84;
            Q84=makeQuery(id+"F4.imprint","IMPRINT",FACE,{"disambiguationData":[TD([[makeQuery(id+"F4.imprint","IMPRINT",EDGE,{"derivedFrom":sQuery(id+"F4.wireOp",EDGE,"E93")}),1.0]])]});
            var Q85;
            Q85=makeQuery(id+"F4.imprint","IMPRINT",FACE,{"disambiguationData":[TD([[makeQuery(id+"F4.imprint","IMPRINT",EDGE,{"derivedFrom":sQuery(id+"F4.wireOp",EDGE,"E51")}),1.0]])]});
            var Q86;
            Q86=makeQuery(id+"F4.imprint","IMPRINT",FACE,{"disambiguationData":[TD([[makeQuery(id+"F4.imprint","IMPRINT",EDGE,{"derivedFrom":sQuery(id+"F4.wireOp",EDGE,"E77")}),1.0]])]});
            var Q87;
            Q87=makeQuery(id+"F4.imprint","IMPRINT",FACE,{"disambiguationData":[TD([[makeQuery(id+"F4.imprint","IMPRINT",EDGE,{"derivedFrom":sQuery(id+"F4.wireOp",EDGE,"E61")}),1.0]])]});
            var Q88;
            Q88=makeQuery(id+"F4.imprint","IMPRINT",FACE,{"disambiguationData":[TD([[makeQuery(id+"F4.imprint","IMPRINT",EDGE,{"derivedFrom":sQuery(id+"F4.wireOp",EDGE,"E35")}),1.0]])]});
            var Q89;
            Q89=makeQuery(id+"F4.imprint","IMPRINT",FACE,{"disambiguationData":[TD([[makeQuery(id+"F4.imprint","IMPRINT",EDGE,{"derivedFrom":sQuery(id+"F4.wireOp",EDGE,"E45")}),1.0]])]});
            var Q90;
            Q90=makeQuery(id+"F4.imprint","IMPRINT",FACE,{"disambiguationData":[TD([[makeQuery(id+"F4.imprint","IMPRINT",EDGE,{"derivedFrom":sQuery(id+"F4.wireOp",EDGE,"E131")}),1.0]])]});
            var Q91;
            Q91=makeQuery(id+"F4.imprint","IMPRINT",FACE,{"disambiguationData":[TD([[makeQuery(id+"F4.imprint","IMPRINT",EDGE,{"derivedFrom":sQuery(id+"F4.wireOp",EDGE,"E141")}),1.0]])]});
            var Q92;
            Q92=makeQuery(id+"F4.imprint","IMPRINT",FACE,{"disambiguationData":[TD([[makeQuery(id+"F4.imprint","IMPRINT",EDGE,{"derivedFrom":sQuery(id+"F4.wireOp",EDGE,"E115")}),1.0]])]});
            var Q93;
            Q93=makeQuery(id+"F4.imprint","IMPRINT",FACE,{"disambiguationData":[TD([[makeQuery(id+"F4.imprint","IMPRINT",EDGE,{"derivedFrom":sQuery(id+"F4.wireOp",EDGE,"E125")}),1.0]])]});
            var Q94;
            Q94=makeQuery(id+"F4.imprint","IMPRINT",FACE,{"disambiguationData":[TD([[makeQuery(id+"F4.imprint","IMPRINT",EDGE,{"derivedFrom":sQuery(id+"F4.wireOp",EDGE,"E83")}),1.0]])]});
            var Q95;
            Q95=makeQuery(id+"F4.imprint","IMPRINT",FACE,{"disambiguationData":[TD([[makeQuery(id+"F4.imprint","IMPRINT",EDGE,{"derivedFrom":sQuery(id+"F4.wireOp",EDGE,"E99")}),1.0]])]});
            var Q96;
            Q96=makeQuery(id+"F4.imprint","IMPRINT",FACE,{"disambiguationData":[TD([[makeQuery(id+"F4.imprint","IMPRINT",EDGE,{"derivedFrom":sQuery(id+"F4.wireOp",EDGE,"E109")}),1.0]])]});
            var Q97;
            Q97=makeQuery(id+"F4.imprint","IMPRINT",FACE,{"disambiguationData":[TD([[makeQuery(id+"F4.imprint","IMPRINT",EDGE,{"derivedFrom":sQuery(id+"F4.wireOp",EDGE,"E30")}),1.0]])]});
            var Q98;
            Q98=makeQuery(id+"F4.imprint","IMPRINT",FACE,{"disambiguationData":[TD([[makeQuery(id+"F4.imprint","IMPRINT",EDGE,{"derivedFrom":sQuery(id+"F4.wireOp",EDGE,"E94")}),1.0]])]});
            var Q99;
            Q99=makeQuery(id+"F4.imprint","IMPRINT",FACE,{"disambiguationData":[TD([[makeQuery(id+"F4.imprint","IMPRINT",EDGE,{"derivedFrom":sQuery(id+"F4.wireOp",EDGE,"E78")}),1.0]])]});
            var Q100;
            Q100=makeQuery(id+"F4.imprint","IMPRINT",FACE,{"disambiguationData":[TD([[makeQuery(id+"F4.imprint","IMPRINT",EDGE,{"derivedFrom":sQuery(id+"F4.wireOp",EDGE,"E62")}),1.0]])]});
            var Q101;
            Q101=makeQuery(id+"F4.imprint","IMPRINT",FACE,{"disambiguationData":[TD([[makeQuery(id+"F4.imprint","IMPRINT",EDGE,{"derivedFrom":sQuery(id+"F4.wireOp",EDGE,"E46")}),1.0]])]});
            var Q102;
            Q102=makeQuery(id+"F4.imprint","IMPRINT",FACE,{"disambiguationData":[TD([[makeQuery(id+"F4.imprint","IMPRINT",EDGE,{"derivedFrom":sQuery(id+"F4.wireOp",EDGE,"E142")}),1.0]])]});
            var Q103;
            Q103=makeQuery(id+"F4.imprint","IMPRINT",FACE,{"disambiguationData":[TD([[makeQuery(id+"F4.imprint","IMPRINT",EDGE,{"derivedFrom":sQuery(id+"F4.wireOp",EDGE,"E126")}),1.0]])]});
            var Q104;
            Q104=makeQuery(id+"F4.imprint","IMPRINT",FACE,{"disambiguationData":[TD([[makeQuery(id+"F4.imprint","IMPRINT",EDGE,{"derivedFrom":sQuery(id+"F4.wireOp",EDGE,"E110")}),1.0]])]});
            var Q105;
            Q105=makeQuery(id+"F4.imprint","IMPRINT",FACE,{"disambiguationData":[TD([[makeQuery(id+"F4.imprint","IMPRINT",EDGE,{"derivedFrom":sQuery(id+"F4.wireOp",EDGE,"E49")}),1.0]])]});
            var Q106;
            Q106=makeQuery(id+"F4.imprint","IMPRINT",FACE,{"disambiguationData":[TD([[makeQuery(id+"F4.imprint","IMPRINT",EDGE,{"derivedFrom":sQuery(id+"F4.wireOp",EDGE,"E33")}),1.0]])]});
            var Q107;
            Q107=makeQuery(id+"F4.imprint","IMPRINT",FACE,{"disambiguationData":[TD([[makeQuery(id+"F4.imprint","IMPRINT",EDGE,{"derivedFrom":sQuery(id+"F4.wireOp",EDGE,"E113")}),1.0]])]});
            var Q108;
            Q108=makeQuery(id+"F4.imprint","IMPRINT",FACE,{"disambiguationData":[TD([[makeQuery(id+"F4.imprint","IMPRINT",EDGE,{"derivedFrom":sQuery(id+"F4.wireOp",EDGE,"E97")}),1.0]])]});
            var Q109;
            Q109=makeQuery(id+"F4.imprint","IMPRINT",FACE,{"disambiguationData":[TD([[makeQuery(id+"F4.imprint","IMPRINT",EDGE,{"derivedFrom":sQuery(id+"F4.wireOp",EDGE,"E129")}),1.0]])]});
            var Q110;
            Q110=makeQuery(id+"F4.imprint","IMPRINT",FACE,{"disambiguationData":[TD([[makeQuery(id+"F4.imprint","IMPRINT",EDGE,{"derivedFrom":sQuery(id+"F4.wireOp",EDGE,"E19")}),1.0]])]});
            var Q111;
            Q111=makeQuery(id+"F4.imprint","IMPRINT",FACE,{"disambiguationData":[TD([[makeQuery(id+"F4.imprint","IMPRINT",EDGE,{"derivedFrom":sQuery(id+"F4.wireOp",EDGE,"E17")}),1.0]])]});
            var Q112;
            Q112=makeQuery(id+"F4.imprint","IMPRINT",FACE,{"disambiguationData":[TD([[makeQuery(id+"F4.imprint","IMPRINT",EDGE,{"derivedFrom":sQuery(id+"F4.wireOp",EDGE,"E18")}),1.0]])]});
            var Q113;
            Q113=makeQuery(id+"F4.imprint","IMPRINT",FACE,{"disambiguationData":[TD([[makeQuery(id+"F4.imprint","IMPRINT",EDGE,{"derivedFrom":sQuery(id+"F4.wireOp",EDGE,"E4")}),1.0]])]});
            var Q114;
            Q114=makeQuery(id+"F4.imprint","IMPRINT",FACE,{"disambiguationData":[TD([[makeQuery(id+"F4.imprint","IMPRINT",EDGE,{"derivedFrom":sQuery(id+"F4.wireOp",EDGE,"E5")}),1.0]])]});
            var Q115;
            Q115=makeQuery(id+"F4.imprint","IMPRINT",FACE,{"disambiguationData":[TD([[makeQuery(id+"F4.imprint","IMPRINT",EDGE,{"derivedFrom":sQuery(id+"F4.wireOp",EDGE,"E6")}),1.0]])]});
            var Q116;
            Q116=makeQuery(id+"F4.imprint","IMPRINT",FACE,{"disambiguationData":[TD([[makeQuery(id+"F4.imprint","IMPRINT",EDGE,{"derivedFrom":sQuery(id+"F4.wireOp",EDGE,"E31")}),1.0]])]});
            var Q117;
            Q117=makeQuery(id+"F4.imprint","IMPRINT",FACE,{"disambiguationData":[TD([[makeQuery(id+"F4.imprint","IMPRINT",EDGE,{"derivedFrom":sQuery(id+"F4.wireOp",EDGE,"E7")}),1.0]])]});
            var Q118;
            Q118=makeQuery(id+"F4.imprint","IMPRINT",FACE,{"disambiguationData":[TD([[makeQuery(id+"F4.imprint","IMPRINT",EDGE,{"derivedFrom":sQuery(id+"F4.wireOp",EDGE,"E95")}),1.0]])]});
            var Q119;
            Q119=makeQuery(id+"F4.imprint","IMPRINT",FACE,{"disambiguationData":[TD([[makeQuery(id+"F4.imprint","IMPRINT",EDGE,{"derivedFrom":sQuery(id+"F4.wireOp",EDGE,"E79")}),1.0]])]});
            var Q120;
            Q120=makeQuery(id+"F4.imprint","IMPRINT",FACE,{"disambiguationData":[TD([[makeQuery(id+"F4.imprint","IMPRINT",EDGE,{"derivedFrom":sQuery(id+"F4.wireOp",EDGE,"E8")}),1.0]])]});
            var Q121;
            Q121=makeQuery(id+"F4.imprint","IMPRINT",FACE,{"disambiguationData":[TD([[makeQuery(id+"F4.imprint","IMPRINT",EDGE,{"derivedFrom":sQuery(id+"F4.wireOp",EDGE,"E63")}),1.0]])]});
            var Q122;
            Q122=makeQuery(id+"F4.imprint","IMPRINT",FACE,{"disambiguationData":[TD([[makeQuery(id+"F4.imprint","IMPRINT",EDGE,{"derivedFrom":sQuery(id+"F4.wireOp",EDGE,"E47")}),1.0]])]});
            var Q123;
            Q123=makeQuery(id+"F4.imprint","IMPRINT",FACE,{"disambiguationData":[TD([[makeQuery(id+"F4.imprint","IMPRINT",EDGE,{"derivedFrom":sQuery(id+"F4.wireOp",EDGE,"E143")}),1.0]])]});
            var Q124;
            Q124=makeQuery(id+"F4.imprint","IMPRINT",FACE,{"disambiguationData":[TD([[makeQuery(id+"F4.imprint","IMPRINT",EDGE,{"derivedFrom":sQuery(id+"F4.wireOp",EDGE,"E9")}),1.0]])]});
            var Q125;
            Q125=makeQuery(id+"F4.imprint","IMPRINT",FACE,{"disambiguationData":[TD([[makeQuery(id+"F4.imprint","IMPRINT",EDGE,{"derivedFrom":sQuery(id+"F4.wireOp",EDGE,"E127")}),1.0]])]});
            var Q126;
            Q126=makeQuery(id+"F4.imprint","IMPRINT",FACE,{"disambiguationData":[TD([[makeQuery(id+"F4.imprint","IMPRINT",EDGE,{"derivedFrom":sQuery(id+"F4.wireOp",EDGE,"E111")}),1.0]])]});
            var Q127;
            Q127=makeQuery(id+"F4.imprint","IMPRINT",FACE,{"disambiguationData":[TD([[makeQuery(id+"F4.imprint","IMPRINT",EDGE,{"derivedFrom":sQuery(id+"F4.wireOp",EDGE,"E10")}),1.0]])]});
            var Q128;
            Q128=makeQuery(id+"F4.imprint","IMPRINT",FACE,{"disambiguationData":[TD([[makeQuery(id+"F4.imprint","IMPRINT",EDGE,{"derivedFrom":sQuery(id+"F4.wireOp",EDGE,"E11")}),1.0]])]});
            var Q129;
            Q129=makeQuery(id+"F4.imprint","IMPRINT",FACE,{"disambiguationData":[TD([[makeQuery(id+"F4.imprint","IMPRINT",EDGE,{"derivedFrom":sQuery(id+"F4.wireOp",EDGE,"E12")}),1.0]])]});
            var Q130;
            Q130=makeQuery(id+"F4.imprint","IMPRINT",FACE,{"disambiguationData":[TD([[makeQuery(id+"F4.imprint","IMPRINT",EDGE,{"derivedFrom":sQuery(id+"F4.wireOp",EDGE,"E13")}),1.0]])]});
            var Q131;
            Q131=makeQuery(id+"F4.imprint","IMPRINT",FACE,{"disambiguationData":[TD([[makeQuery(id+"F4.imprint","IMPRINT",EDGE,{"derivedFrom":sQuery(id+"F4.wireOp",EDGE,"E50")}),1.0]])]});
            var Q132;
            Q132=makeQuery(id+"F4.imprint","IMPRINT",FACE,{"disambiguationData":[TD([[makeQuery(id+"F4.imprint","IMPRINT",EDGE,{"derivedFrom":sQuery(id+"F4.wireOp",EDGE,"E34")}),1.0]])]});
            var Q133;
            Q133=makeQuery(id+"F4.imprint","IMPRINT",FACE,{"disambiguationData":[TD([[makeQuery(id+"F4.imprint","IMPRINT",EDGE,{"derivedFrom":sQuery(id+"F4.wireOp",EDGE,"E14")}),1.0]])]});
            var Q134;
            Q134=makeQuery(id+"F4.imprint","IMPRINT",FACE,{"disambiguationData":[TD([[makeQuery(id+"F4.imprint","IMPRINT",EDGE,{"derivedFrom":sQuery(id+"F4.wireOp",EDGE,"E114")}),1.0]])]});
            var Q135;
            Q135=makeQuery(id+"F4.imprint","IMPRINT",FACE,{"disambiguationData":[TD([[makeQuery(id+"F4.imprint","IMPRINT",EDGE,{"derivedFrom":sQuery(id+"F4.wireOp",EDGE,"E98")}),1.0]])]});
            var Q136;
            Q136=makeQuery(id+"F4.imprint","IMPRINT",FACE,{"disambiguationData":[TD([[makeQuery(id+"F4.imprint","IMPRINT",EDGE,{"derivedFrom":sQuery(id+"F4.wireOp",EDGE,"E82")}),1.0]])]});
            var Q137;
            Q137=makeQuery(id+"F4.imprint","IMPRINT",FACE,{"disambiguationData":[TD([[makeQuery(id+"F4.imprint","IMPRINT",EDGE,{"derivedFrom":sQuery(id+"F4.wireOp",EDGE,"E15")}),1.0]])]});
            var Q138;
            Q138=makeQuery(id+"F4.imprint","IMPRINT",FACE,{"disambiguationData":[TD([[makeQuery(id+"F4.imprint","IMPRINT",EDGE,{"derivedFrom":sQuery(id+"F4.wireOp",EDGE,"E66")}),1.0]])]});
            var Q139;
            Q139=makeQuery(id+"F4.imprint","IMPRINT",FACE,{"disambiguationData":[TD([[makeQuery(id+"F4.imprint","IMPRINT",EDGE,{"derivedFrom":sQuery(id+"F4.wireOp",EDGE,"E146")}),1.0]])]});
            var Q140;
            Q140=makeQuery(id+"F4.imprint","IMPRINT",FACE,{"disambiguationData":[TD([[makeQuery(id+"F4.imprint","IMPRINT",EDGE,{"derivedFrom":sQuery(id+"F4.wireOp",EDGE,"E16")}),1.0]])]});
            var Q141;
            Q141=makeQuery(id+"F4.imprint","IMPRINT",FACE,{"disambiguationData":[TD([[makeQuery(id+"F4.imprint","IMPRINT",EDGE,{"derivedFrom":sQuery(id+"F4.wireOp",EDGE,"E130")}),1.0]])]});
            var Q142;
            Q142=makeQuery(id+"F4.imprint","IMPRINT",FACE,{"disambiguationData":[TD([[makeQuery(id+"F4.imprint","IMPRINT",EDGE,{"derivedFrom":sQuery(id+"F4.wireOp",EDGE,"E32")}),1.0]])]});
            var Q143;
            Q143=makeQuery(id+"F4.imprint","IMPRINT",FACE,{"disambiguationData":[TD([[makeQuery(id+"F4.imprint","IMPRINT",EDGE,{"derivedFrom":sQuery(id+"F4.wireOp",EDGE,"E96")}),1.0]])]});
            var Q144;
            Q144=makeQuery(id+"F4.imprint","IMPRINT",FACE,{"disambiguationData":[TD([[makeQuery(id+"F4.imprint","IMPRINT",EDGE,{"derivedFrom":sQuery(id+"F4.wireOp",EDGE,"E80")}),1.0]])]});
            var Q145;
            Q145=makeQuery(id+"F4.imprint","IMPRINT",FACE,{"disambiguationData":[TD([[makeQuery(id+"F4.imprint","IMPRINT",EDGE,{"derivedFrom":sQuery(id+"F4.wireOp",EDGE,"E64")}),1.0]])]});
            var Q146;
            Q146=makeQuery(id+"F4.imprint","IMPRINT",FACE,{"disambiguationData":[TD([[makeQuery(id+"F4.imprint","IMPRINT",EDGE,{"derivedFrom":sQuery(id+"F4.wireOp",EDGE,"E48")}),1.0]])]});
            var Q147;
            Q147=makeQuery(id+"F4.imprint","IMPRINT",FACE,{"disambiguationData":[TD([[makeQuery(id+"F4.imprint","IMPRINT",EDGE,{"derivedFrom":sQuery(id+"F4.wireOp",EDGE,"E144")}),1.0]])]});
            var Q148;
            Q148=makeQuery(id+"F4.imprint","IMPRINT",FACE,{"disambiguationData":[TD([[makeQuery(id+"F4.imprint","IMPRINT",EDGE,{"derivedFrom":sQuery(id+"F4.wireOp",EDGE,"E128")}),1.0]])]});
            var Q149;
            Q149=makeQuery(id+"F4.imprint","IMPRINT",FACE,{"disambiguationData":[TD([[makeQuery(id+"F4.imprint","IMPRINT",EDGE,{"derivedFrom":sQuery(id+"F4.wireOp",EDGE,"E112")}),1.0]])]});
            var Q150;
            Q150=sQuery(id+"F4.wireOp",EDGE,"E92");
            var Q151;
            Q151=sQuery(id+"F4.wireOp",EDGE,"E28");
            var Q152;
            Q152=sQuery(id+"F4.wireOp",EDGE,"E76");
            var Q153;
            Q153=sQuery(id+"F4.wireOp",EDGE,"E123");
            var Q154;
            Q154=sQuery(id+"F4.wireOp",EDGE,"E33");
            var Q155;
            Q155=sQuery(id+"F4.wireOp",EDGE,"E59");
            var Q156;
            Q156=sQuery(id+"F4.wireOp",EDGE,"E43");
            var Q157;
            Q157=sQuery(id+"F4.wireOp",EDGE,"E66");
            var Q158;
            Q158=sQuery(id+"F4.wireOp",EDGE,"E113");
            var Q159;
            Q159=sQuery(id+"F4.wireOp",EDGE,"E130");
            var Q160;
            Q160=sQuery(id+"F4.wireOp",EDGE,"E75");
            var Q161;
            Q161=sQuery(id+"F4.wireOp",EDGE,"E139");
            var Q162;
            Q162=sQuery(id+"F4.wireOp",EDGE,"E61");
            var Q163;
            Q163=sQuery(id+"F4.wireOp",EDGE,"E91");
            var Q164;
            Q164=sQuery(id+"F4.wireOp",EDGE,"E98");
            var Q165;
            Q165=sQuery(id+"F4.wireOp",EDGE,"E30");
            var Q166;
            Q166=sQuery(id+"F4.wireOp",EDGE,"E27");
            var Q167;
            Q167=sQuery(id+"F4.wireOp",EDGE,"E62");
            var Q168;
            Q168=sQuery(id+"F4.wireOp",EDGE,"E107");
            var Q169;
            Q169=sQuery(id+"F4.wireOp",EDGE,"E29");
            var Q170;
            Q170=sQuery(id+"F4.wireOp",EDGE,"E46");
            var Q171;
            Q171=sQuery(id+"F4.wireOp",EDGE,"E77");
            var Q172;
            Q172=sQuery(id+"F4.wireOp",EDGE,"E110");
            var Q173;
            Q173=sQuery(id+"F4.wireOp",EDGE,"E146");
            var Q174;
            Q174=sQuery(id+"F4.wireOp",EDGE,"E94");
            var Q175;
            Q175=sQuery(id+"F4.wireOp",EDGE,"E44");
            var Q176;
            Q176=sQuery(id+"F4.wireOp",EDGE,"E60");
            var Q177;
            Q177=sQuery(id+"F4.wireOp",EDGE,"E26");
            var Q178;
            Q178=sQuery(id+"F4.wireOp",EDGE,"E78");
            var Q179;
            Q179=sQuery(id+"F4.wireOp",EDGE,"E140");
            var Q180;
            Q180=sQuery(id+"F4.wireOp",EDGE,"E124");
            var Q181;
            Q181=sQuery(id+"F4.wireOp",EDGE,"E96");
            var Q182;
            Q182=sQuery(id+"F4.wireOp",EDGE,"E32");
            var Q183;
            Q183=sQuery(id+"F4.wireOp",EDGE,"E93");
            var Q184;
            Q184=sQuery(id+"F4.wireOp",EDGE,"E80");
            var Q185;
            Q185=sQuery(id+"F4.wireOp",EDGE,"E64");
            var Q186;
            Q186=sQuery(id+"F4.wireOp",EDGE,"E48");
            var Q187;
            Q187=sQuery(id+"F4.wireOp",EDGE,"E144");
            var Q188;
            Q188=sQuery(id+"F4.wireOp",EDGE,"E137");
            var Q189;
            Q189=sQuery(id+"F4.wireOp",EDGE,"E108");
            var Q190;
            Q190=sQuery(id+"F4.wireOp",EDGE,"E128");
            var Q191;
            Q191=sQuery(id+"F4.wireOp",EDGE,"E45");
            var Q192;
            Q192=sQuery(id+"F4.wireOp",EDGE,"E125");
            var Q193;
            Q193=sQuery(id+"F4.wireOp",EDGE,"E141");
            var Q194;
            Q194=sQuery(id+"F4.wireOp",EDGE,"E50");
            var Q195;
            Q195=sQuery(id+"F4.wireOp",EDGE,"E109");
            var Q196;
            Q196=sQuery(id+"F4.wireOp",EDGE,"E112");
            var Q197;
            Q197=sQuery(id+"F4.wireOp",EDGE,"E132");
            var Q198;
            Q198=sQuery(id+"F4.wireOp",EDGE,"E81");
            var Q199;
            Q199=sQuery(id+"F4.wireOp",EDGE,"E82");
            var Q200;
            Q200=sQuery(id+"F4.wireOp",EDGE,"E42");
            var Q201;
            Q201=sQuery(id+"F4.wireOp",EDGE,"E138");
            var Q202;
            Q202=sQuery(id+"F4.wireOp",EDGE,"E58");
            var Q203;
            Q203=sQuery(id+"F4.wireOp",EDGE,"E34");
            var Q204;
            Q204=sQuery(id+"F4.wireOp",EDGE,"E74");
            var Q205;
            Q205=sQuery(id+"F4.wireOp",EDGE,"E122");
            var Q206;
            Q206=sQuery(id+"F4.wireOp",EDGE,"E114");
            var Q207;
            Q207=sQuery(id+"F4.wireOp",EDGE,"E126");
            var Q208;
            Q208=sQuery(id+"F4.wireOp",EDGE,"E142");
            var Q209;
            Q209=sQuery(id+"F4.wireOp",EDGE,"E51");
            var Q210;
            Q210=sQuery(id+"F4.wireOp",EDGE,"E106");
            var Q211;
            Q211=sQuery(id+"F4.wireOp",EDGE,"E115");
            var Q212;
            Q212=sQuery(id+"F4.wireOp",EDGE,"E35");
            var Q213;
            Q213=sQuery(id+"F4.wireOp",EDGE,"E99");
            var Q214;
            Q214=sQuery(id+"F4.wireOp",EDGE,"E97");
            var Q215;
            Q215=sQuery(id+"F4.wireOp",EDGE,"E83");
            var Q216;
            Q216=sQuery(id+"F4.wireOp",EDGE,"E67");
            var Q217;
            Q217=sQuery(id+"F4.wireOp",EDGE,"E147");
            var Q218;
            Q218=sQuery(id+"F4.wireOp",EDGE,"E131");
            var Q219;
            Q219=sQuery(id+"F4.wireOp",EDGE,"E52");
            var Q220;
            Q220=sQuery(id+"F4.wireOp",EDGE,"E36");
            var Q221;
            Q221=sQuery(id+"F4.wireOp",EDGE,"E20");
            var Q222;
            Q222=sQuery(id+"F4.wireOp",EDGE,"E65");
            var Q223;
            Q223=sQuery(id+"F4.wireOp",EDGE,"E90");
            var Q224;
            Q224=sQuery(id+"F4.wireOp",EDGE,"E95");
            var Q225;
            Q225=sQuery(id+"F4.wireOp",EDGE,"E31");
            var Q226;
            Q226=sQuery(id+"F4.wireOp",EDGE,"E63");
            var Q227;
            Q227=sQuery(id+"F4.wireOp",EDGE,"E79");
            var Q228;
            Q228=sQuery(id+"F4.wireOp",EDGE,"E47");
            var Q229;
            Q229=sQuery(id+"F4.wireOp",EDGE,"E143");
            var Q230;
            Q230=sQuery(id+"F4.wireOp",EDGE,"E127");
            var Q231;
            Q231=sQuery(id+"F4.wireOp",EDGE,"E116");
            var Q232;
            Q232=sQuery(id+"F4.wireOp",EDGE,"E100");
            var Q233;
            Q233=sQuery(id+"F4.wireOp",EDGE,"E111");
            var Q234;
            Q234=sQuery(id+"F4.wireOp",EDGE,"E49");
            var Q235;
            Q235=sQuery(id+"F4.wireOp",EDGE,"E84");
            var Q236;
            Q236=sQuery(id+"F4.wireOp",EDGE,"E148");
            var Q237;
            Q237=sQuery(id+"F4.wireOp",EDGE,"E68");
            var Q238;
            Q238=sQuery(id+"F4.wireOp",EDGE,"E101");
            var Q239;
            Q239=sQuery(id+"F4.wireOp",EDGE,"E117");
            var Q240;
            Q240=sQuery(id+"F4.wireOp",EDGE,"E85");
            var Q241;
            Q241=sQuery(id+"F4.wireOp",EDGE,"E69");
            var Q242;
            Q242=sQuery(id+"F4.wireOp",EDGE,"E149");
            var Q243;
            Q243=sQuery(id+"F4.wireOp",EDGE,"E133");
            var Q244;
            Q244=sQuery(id+"F4.wireOp",EDGE,"E129");
            var Q245;
            Q245=sQuery(id+"F4.wireOp",EDGE,"E145");
            var Q246;
            Q246=sQuery(id+"F4.wireOp",EDGE,"E53");
            var Q247;
            Q247=sQuery(id+"F4.wireOp",EDGE,"E37");
            var Q248;
            Q248=sQuery(id+"F4.wireOp",EDGE,"E21");
            var Q249;
            Q249=sQuery(id+"F4.wireOp",EDGE,"E150");
            var Q250;
            Q250=sQuery(id+"F4.wireOp",EDGE,"E134");
            var Q251;
            Q251=sQuery(id+"F4.wireOp",EDGE,"E54");
            var Q252;
            Q252=sQuery(id+"F4.wireOp",EDGE,"E38");
            var Q253;
            Q253=sQuery(id+"F4.wireOp",EDGE,"E22");
            var Q254;
            Q254=sQuery(id+"F4.wireOp",EDGE,"E118");
            var Q255;
            Q255=sQuery(id+"F4.wireOp",EDGE,"E86");
            var Q256;
            Q256=sQuery(id+"F4.wireOp",EDGE,"E102");
            var Q257;
            Q257=sQuery(id+"F4.wireOp",EDGE,"E70");
            var Q258;
            Q258=sQuery(id+"F4.wireOp",EDGE,"E55");
            var Q259;
            Q259=sQuery(id+"F4.wireOp",EDGE,"E39");
            var Q260;
            Q260=sQuery(id+"F4.wireOp",EDGE,"E23");
            var Q261;
            Q261=sQuery(id+"F4.wireOp",EDGE,"E119");
            var Q262;
            Q262=sQuery(id+"F4.wireOp",EDGE,"E103");
            var Q263;
            Q263=sQuery(id+"F4.wireOp",EDGE,"E87");
            var Q264;
            Q264=sQuery(id+"F4.wireOp",EDGE,"E151");
            var Q265;
            Q265=sQuery(id+"F4.wireOp",EDGE,"E71");
            var Q266;
            Q266=sQuery(id+"F4.wireOp",EDGE,"E135");
            var Q267;
            Q267=sQuery(id+"F4.wireOp",EDGE,"E17");
            var Q268;
            Q268=sQuery(id+"F4.wireOp",EDGE,"E18");
            var Q269;
            Q269=sQuery(id+"F4.wireOp",EDGE,"E19");
            var Q270;
            Q270=sQuery(id+"F4.wireOp",EDGE,"E4");
            var Q271;
            Q271=sQuery(id+"F4.wireOp",EDGE,"E5");
            var Q272;
            Q272=sQuery(id+"F4.wireOp",EDGE,"E6");
            var Q273;
            Q273=sQuery(id+"F4.wireOp",EDGE,"E7");
            var Q274;
            Q274=sQuery(id+"F4.wireOp",EDGE,"E8");
            var Q275;
            Q275=sQuery(id+"F4.wireOp",EDGE,"E9");
            var Q276;
            Q276=sQuery(id+"F4.wireOp",EDGE,"E10");
            var Q277;
            Q277=sQuery(id+"F4.wireOp",EDGE,"E11");
            var Q278;
            Q278=sQuery(id+"F4.wireOp",EDGE,"E12");
            var Q279;
            Q279=sQuery(id+"F4.wireOp",EDGE,"E13");
            var Q280;
            Q280=sQuery(id+"F4.wireOp",EDGE,"E14");
            var Q281;
            Q281=sQuery(id+"F4.wireOp",EDGE,"E56");
            var Q282;
            Q282=sQuery(id+"F4.wireOp",EDGE,"E40");
            var Q283;
            Q283=sQuery(id+"F4.wireOp",EDGE,"E24");
            var Q284;
            Q284=sQuery(id+"F4.wireOp",EDGE,"E15");
            var Q285;
            Q285=sQuery(id+"F4.wireOp",EDGE,"E120");
            var Q286;
            Q286=sQuery(id+"F4.wireOp",EDGE,"E104");
            var Q287;
            Q287=sQuery(id+"F4.wireOp",EDGE,"E88");
            var Q288;
            Q288=sQuery(id+"F4.wireOp",EDGE,"E16");
            var Q289;
            Q289=sQuery(id+"F4.wireOp",EDGE,"E72");
            var Q290;
            Q290=sQuery(id+"F4.wireOp",EDGE,"E152");
            var Q291;
            Q291=sQuery(id+"F4.wireOp",EDGE,"E136");
            var Q292;
            Q292=sQuery(id+"F4.wireOp",EDGE,"E57");
            var Q293;
            Q293=sQuery(id+"F4.wireOp",EDGE,"E25");
            var Q294;
            Q294=sQuery(id+"F4.wireOp",EDGE,"E41");
            var Q295;
            Q295=sQuery(id+"F4.wireOp",EDGE,"E121");
            var Q296;
            Q296=sQuery(id+"F4.wireOp",EDGE,"E105");
            var Q297;
            Q297=sQuery(id+"F4.wireOp",EDGE,"E89");
            var Q298;
            Q298=sQuery(id+"F4.wireOp",EDGE,"E73");
            var Q299;
            Q299=sQuery(id+"F4.wireOp",EDGE,"E153");
            extrude(context, id + "F5", {"entities" : qUnion([Q0, Q1, Q2, Q3, Q4, Q5, Q6, Q7, Q8, Q9, Q10, Q11, Q12, Q13, Q14, Q15, Q16, Q17, Q18, Q19, Q20, Q21, Q22, Q23, Q24, Q25, Q26, Q27, Q28, Q29, Q30, Q31, Q32, Q33, Q34, Q35, Q36, Q37, Q38, Q39, Q40, Q41, Q42, Q43, Q44, Q45, Q46, Q47, Q48, Q49, Q50, Q51, Q52, Q53, Q54, Q55, Q56, Q57, Q58, Q59, Q60, Q61, Q62, Q63, Q64, Q65, Q66, Q67, Q68, Q69, Q70, Q71, Q72, Q73, Q74, Q75, Q76, Q77, Q78, Q79, Q80, Q81, Q82, Q83, Q84, Q85, Q86, Q87, Q88, Q89, Q90, Q91, Q92, Q93, Q94, Q95, Q96, Q97, Q98, Q99, Q100, Q101, Q102, Q103, Q104, Q105, Q106, Q107, Q108, Q109, Q110, Q111, Q112, Q113, Q114, Q115, Q116, Q117, Q118, Q119, Q120, Q121, Q122, Q123, Q124, Q125, Q126, Q127, Q128, Q129, Q130, Q131, Q132, Q133, Q134, Q135, Q136, Q137, Q138, Q139, Q140, Q141, Q142, Q143, Q144, Q145, Q146, Q147, Q148, Q149]), "operationType" : NewBodyOperationType.REMOVE, "surfaceEntities" : qUnion([Q150, Q151, Q152, Q153, Q154, Q155, Q156, Q157, Q158, Q159, Q160, Q161, Q162, Q163, Q164, Q165, Q166, Q167, Q168, Q169, Q170, Q171, Q172, Q173, Q174, Q175, Q176, Q177, Q178, Q179, Q180, Q181, Q182, Q183, Q184, Q185, Q186, Q187, Q188, Q189, Q190, Q191, Q192, Q193, Q194, Q195, Q196, Q197, Q198, Q199, Q200, Q201, Q202, Q203, Q204, Q205, Q206, Q207, Q208, Q209, Q210, Q211, Q212, Q213, Q214, Q215, Q216, Q217, Q218, Q219, Q220, Q221, Q222, Q223, Q224, Q225, Q226, Q227, Q228, Q229, Q230, Q231, Q232, Q233, Q234, Q235, Q236, Q237, Q238, Q239, Q240, Q241, Q242, Q243, Q244, Q245, Q246, Q247, Q248, Q249, Q250, Q251, Q252, Q253, Q254, Q255, Q256, Q257, Q258, Q259, Q260, Q261, Q262, Q263, Q264, Q265, Q266, Q267, Q268, Q269, Q270, Q271, Q272, Q273, Q274, Q275, Q276, Q277, Q278, Q279, Q280, Q281, Q282, Q283, Q284, Q285, Q286, Q287, Q288, Q289, Q290, Q291, Q292, Q293, Q294, Q295, Q296, Q297, Q298, Q299]), "depth" : 7.5 * mm});
        }
    });
